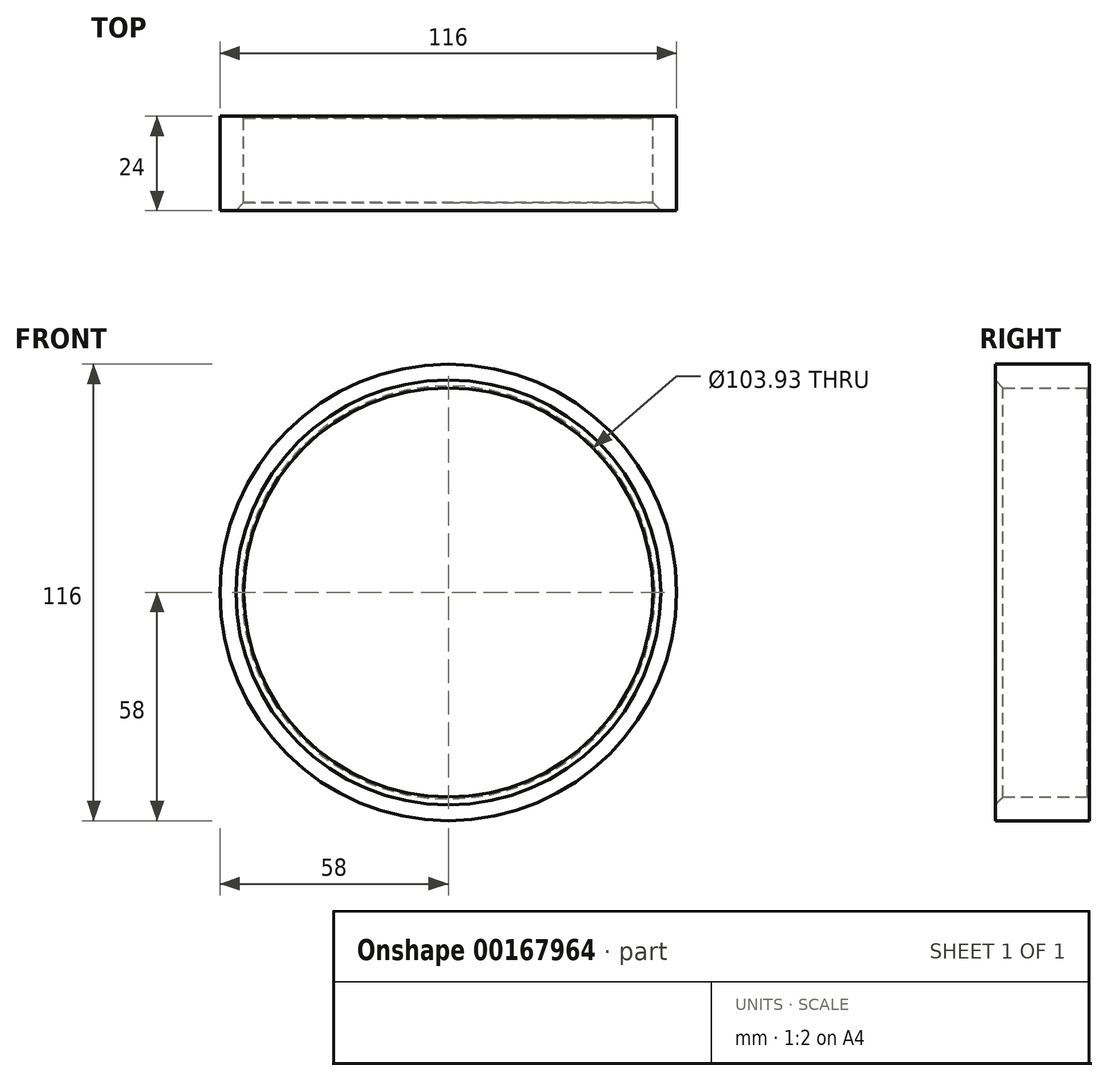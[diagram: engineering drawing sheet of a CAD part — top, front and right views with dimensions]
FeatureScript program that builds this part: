
annotation { "Feature Type Name" : "Feature", "Feature Type Description" : "" }
export const myFeature = defineFeature(function(context is Context, id is Id, definition is map)
    precondition{}
    {
        {
            var Q0;
            Q0=qCreatedBy(makeId("Front.planeOp"),FACE);
            var sketch = newSketch(context, id + "F0", { "sketchPlane" : qUnion([Q0])});
            skCircle(sketch, "E0", {"center": v(0, 0) * mm, "radius": 58 * mm});
            skCircle(sketch, "E1", {"center": v(0, 0) * mm, "radius": 51.97 * mm});
            skSolve(sketch);
        }
        {
            var Q0;
            Q0=makeQuery(id+"F0.imprint","IMPRINT",FACE,{"disambiguationData":[TD([[makeQuery(id+"F0.imprint","IMPRINT",EDGE,{"derivedFrom":sQuery(id+"F0.wireOp",EDGE,"E0")}),1.0]])]});
            extrude(context, id + "F1", {"entities" : qUnion([Q0]), "depth" : 24 * mm, "offsetDistance" : 25 * mm});
        }
        {
            var Q0;
            Q0=makeQuery(id+"F1.opExtrude","CAP_EDGE",EDGE,{"disambiguationData":[OSD([sQuery(id+"F0.wireOp",EDGE,"E1")])],"isStart":false});
            chamfer(context, id + "F2", {"entities" : qUnion([Q0]), "width" : 2 * mm, "tangentPropagation" : true});
        }
        {
            var Q0;
            Q0=makeQuery(id+"F1.opExtrude","CAP_EDGE",EDGE,{"disambiguationData":[OSD([sQuery(id+"F0.wireOp",EDGE,"E1")])],"isStart":true});
            chamfer(context, id + "F3", {"entities" : qUnion([Q0]), "width" : .5 * mm, "tangentPropagation" : true});
        }
    });
